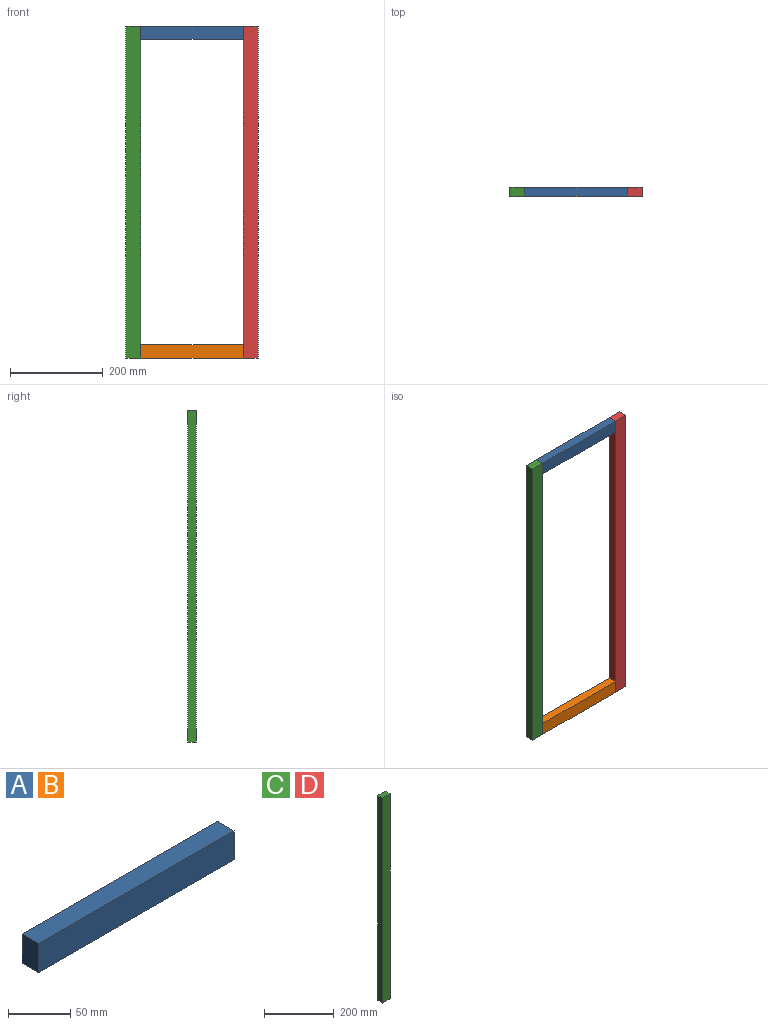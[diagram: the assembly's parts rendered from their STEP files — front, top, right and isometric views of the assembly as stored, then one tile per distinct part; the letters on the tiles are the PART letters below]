
ASSEMBLY  parts=4 mates=9
PART A: 6 faces, bbox 222.3x19.1x28.6 mm
  f0: plane 28.58x19.05mm, normal (-1,0,0), area 544.4mm2, adj f1,f3,f4,f5
  f1: plane 222.25x19.05mm, normal (0,0,-1), area 4233.9mm2, adj f0,f2,f4,f5
  f2: plane 28.58x19.05mm, normal (1,0,0), area 544.4mm2, adj f1,f3,f4,f5
  f3: plane 222.25x19.05mm, normal (0,0,1), area 4233.9mm2, adj f0,f2,f4,f5
  f4: plane 222.25x28.58mm, normal (0,-1,0), area 6350.8mm2, adj f0,f1,f2,f3
  f5: plane 222.25x28.58mm, normal (0,1,0), area 6350.8mm2, adj f0,f1,f2,f3
PART B: same geometry as A
PART C: 6 faces, bbox 31.8x19.1x717.6 mm
  f0: plane 31.75x19.05mm, normal (0,0,-1), area 604.8mm2, adj f1,f3,f4,f5
  f1: plane 717.55x19.05mm, normal (1,0,0), area 13669.3mm2, adj f0,f2,f4,f5
  f2: plane 31.75x19.05mm, normal (0,0,1), area 604.8mm2, adj f1,f3,f4,f5
  f3: plane 717.55x19.05mm, normal (-1,0,0), area 13669.3mm2, adj f0,f2,f4,f5
  f4: plane 717.55x31.75mm, normal (0,-1,0), area 22782.2mm2, adj f0,f1,f2,f3
  f5: plane 717.55x31.75mm, normal (0,1,0), area 22782.2mm2, adj f0,f1,f2,f3
PART D: same geometry as C
PLACE A t=(396.36,8.65,18.6)mm
PLACE B t=(396.36,8.65,-670.37)mm
PLACE C t=(396.36,8.65,18.6)mm
PLACE D t=(650.36,8.65,18.6)mm
MATE planar C.f4 <-> D.f4  axis (0,-1,0) through (380.49,-10.4,-340.17)mm
MATE planar A.f0 <-> C.f1  axis (-1,0,0) through (396.36,-0.88,4.32)mm
MATE planar B.f0 <-> C.f1  axis (-1,0,0) through (396.36,-0.88,-684.66)mm
MATE planar C.f4 <-> A.f4  axis (0,-1,0) through (364.61,-10.4,-340.17)mm
MATE planar D.f3 <-> A.f2  axis (-1,0,0) through (618.61,-0.88,-340.17)mm
MATE planar C.f4 <-> B.f4  axis (0,-1,0) through (380.49,-10.4,-340.17)mm
MATE planar A.f3 <-> C.f2  axis (0,0,1) through (507.49,-0.88,18.6)mm
MATE planar B.f1 <-> C.f0  axis (0,0,-1) through (507.49,-0.88,-698.95)mm
MATE planar D.f2 <-> A.f3  axis (0,0,1) through (634.49,-0.88,18.6)mm
